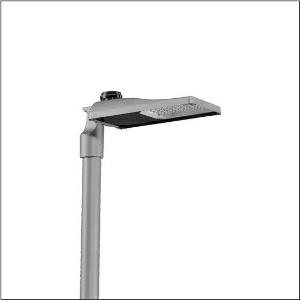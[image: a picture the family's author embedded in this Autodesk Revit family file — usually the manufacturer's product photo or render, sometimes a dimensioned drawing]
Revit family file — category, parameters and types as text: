
# Revit family: streetlight_sl_31_mini___st1_0a_5xh6d3bn08ha_24b0
name_source: partatom
category: Lighting Fixtures
units: mm (PartAtom-declared; Revit-internal decimal feet)

## family parameters
Cut with Voids When Loaded = No
Host = Face
Light Source = No
Part Type = Normal
Room Calculation Point = No
Round Connector Dimension = Use Diameter
Shared = No

## types (1)
- --- (1 x LED, 9240 lm, 68.3 W, 3000K)
    Apparent Load = 68 VA
    CIE Flux Codes = 37 72 97 100 100
    Color Rendering = 70
    Color Temperature = 3000K
    Default Elevation = 1800 mm
    Description = Streetlight SL 31 mini NEMA (7pin) mast luminaire for post-top, side-entry; light control with lens of PMMA; light distribution: ST1.0a, direct asymmetric distribution, for standard-compliant lighting for roads and squares; LED: luminous flux: 9.240lm, light colour: 730, colour temperature: 3000K; luminous efficacy: 135,3lm/W; control: pre-setting: linear dimming characteristic, flexible luminous flux parameterisation, time-dependent luminous flux control, constant luminous flux control, intelligent temperature release in ECG and LED module, overheat protection; luminaire housing, of diecast aluminium, Siteco® metallic grey (DB 702S), corrosivity category C5 high according to DIN EN ISO 12944; cover of toughened safety glass, transparent, opened without tools; mast flange of diecast aluminium, Siteco® metallic grey (DB 702S), spigot size: 76/60mm, mast flange included unmounted; with cable H07RN-F 3x 1.5mm², cable length: 8,5m, connection cable pre-assembled; mains connection: 220..240V, AC, 50/60Hz; power consumption (at start of service life): 68,3W / (at end of service life): 74,8W / (with reduced operation 50%): 29,7W; protection rating (complete): IP66; insulation class (complete): insulation class I (protective earthing); impact resistance: IK10; certification: CE, ENEC, ENEC+, VDE, UKCA; permissible operating ambient temperature for outdoor applications: -40..+50°C; packaging unit: 1 piece

Light Distribution: ST1.0a
    Height = 76 mm
    Lamp = 1 x LED
    Lamp Light Flux = 9240 lm
    Lamp Power = 68.3 W
    Lamp count = 1
    Length = 547 mm
    Luminous efficacy = 135 lm/W
    Manufacturer = Siteco
    ModVariant = No
    Model = 5XH6D3BN08HA
    Number of Poles = 1
    OnlyDefault = Yes
    Power Factor = 1
    Product Name = Streetlight SL 31 mini | ST1.0a
    Product group = mast luminaire | pylon top
    ProductGroupID = 6100
    Protection Class = Protection class I
    Protection Degree = IP 66
    RLX_Detail_Level = 1
    RLX_Emergency_Light_Flux = 0 lm
    RLX_Emergency_Type = 0
    RLX_Emergency_Type_DB = No
    RlxData = <blob elided: 40169 chars, md5=e5bc9a3e>
    Socket = socket
    Standby Power = 0 W
    System Light Flux = 9240 lm
    System Power = 68 W
    Type Comments = factory setting: luminous flux: 100 % | dim-lin: 254 | 693 mA
    Type Image = l_1300322.jpg
    URL = http://relux.com
    VarID = @adj_053720
    Voltage = 0 V
    Weight = 0.00 kg
    Width = 265 mm

## geometry (parser evidence)
native form markers: Blend x4, Sweep x9
no freeform markers — native parametric forms only
